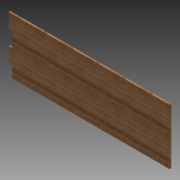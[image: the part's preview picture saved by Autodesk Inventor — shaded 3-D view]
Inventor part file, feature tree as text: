
AUTODESK INVENTOR PART (.ipt)
format: ipt  version: 2012 (Build 160160000, 160)  size: 97,792 bytes
history: native  units: in
note: dims shown in document units (in); Inventor stores cm internally (conversion verified against a paired STEP export)
features: extrude x1, sketch x1
ambient origin geometry x8: Origin, YZ Plane, XZ Plane, XY Plane, X Axis, Y Axis, Z Axis, Center Point
bodies: Solid1 (feature_tree)
feature tree (2):
  extrude  "Extrusion1"  Depth=21.25in
  sketch  "Sketch1"  dims[d0=7.5in d1=21.25in d2=0.25in d3=0.0in d10=0.5in d11=2.0in d12=2.0in d13=2.0in]
